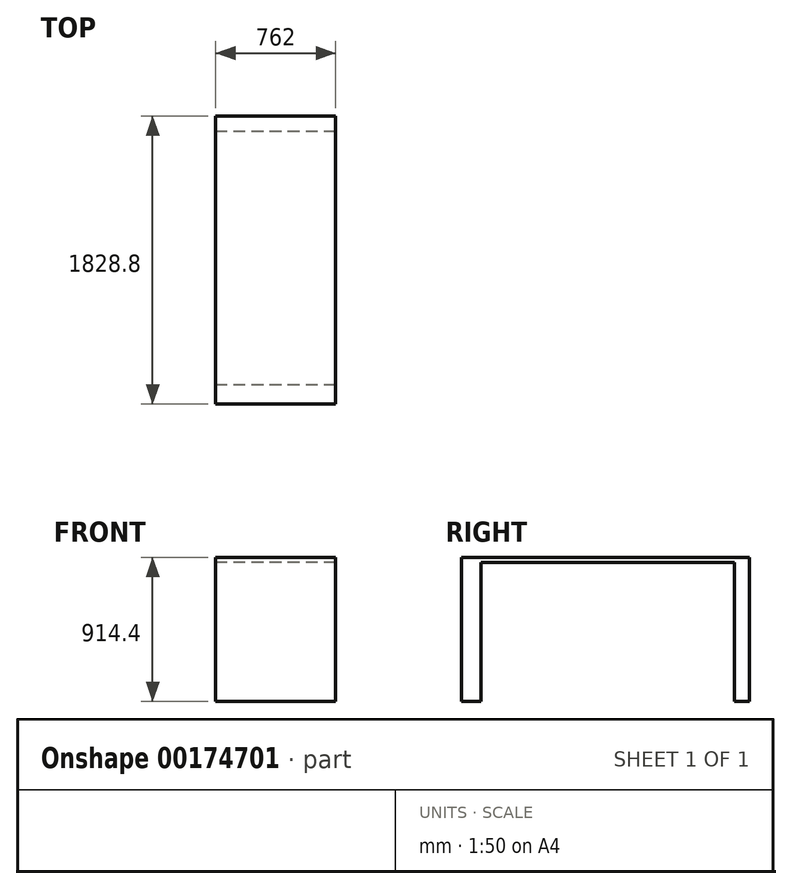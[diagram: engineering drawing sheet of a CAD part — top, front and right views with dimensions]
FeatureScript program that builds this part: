
annotation { "Feature Type Name" : "Feature", "Feature Type Description" : "" }
export const myFeature = defineFeature(function(context is Context, id is Id, definition is map)
    precondition{}
    {
        {
            var Q0;
            Q0=qCreatedBy(makeId("Top.planeOp"),FACE);
            var sketch = newSketch(context, id + "F0", { "sketchPlane" : qUnion([Q0])});
            skLineSegment(sketch, "E0.bottom", {"start": v(381, -914.4) * mm, "end": v(-381, -914.4) * mm});
            skLineSegment(sketch, "E0.top", {"start": v(381, 914.4) * mm, "end": v(-381, 914.4) * mm});
            skLineSegment(sketch, "E0.left", {"start": v(381, -914.4) * mm, "end": v(381, 914.4) * mm});
            skLineSegment(sketch, "E0.right", {"start": v(-381, -914.4) * mm, "end": v(-381, 914.4) * mm});
            skPoint(sketch, "E0.middle", {"position": v(0, 0) * mm});
            skSolve(sketch);
        }
        {
            var Q0;
            Q0 = qSketchRegion(id + "F0", true);
            extrude(context, id + "F1", {"entities" : qUnion([Q0]), "depth" : 914.4 * mm});
        }
        {
            var Q0;
            Q0=makeQuery(id+"F1.opExtrude","SWEPT_FACE",FACE,{"disambiguationData":[OSD([sQuery(id+"F0.wireOp",EDGE,"E0.right")])]});
            var sketch = newSketch(context, id + "F2", { "sketchPlane" : qUnion([Q0])});
            skLineSegment(sketch, "E1.bottom", {"start": v(-817.39, 0) * mm, "end": v(793.52, 0) * mm});
            skLineSegment(sketch, "E1.top", {"start": v(-817.39, 883.48) * mm, "end": v(793.52, 883.48) * mm});
            skLineSegment(sketch, "E1.left", {"start": v(-817.39, 0) * mm, "end": v(-817.39, 883.48) * mm});
            skLineSegment(sketch, "E1.right", {"start": v(793.52, 0) * mm, "end": v(793.52, 883.48) * mm});
            skSolve(sketch);
        }
        {
            var Q0;
            Q0 = qSketchRegion(id + "F2", true);
            extrude(context, id + "F3", {"entities" : qUnion([Q0]), "operationType" : NewBodyOperationType.REMOVE, "endBound" : BoundingType.THROUGH_ALL, "oppositeDirection" : true, "depth" : 25.4 * mm});
        }
    });
